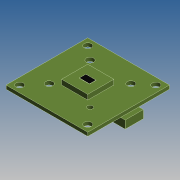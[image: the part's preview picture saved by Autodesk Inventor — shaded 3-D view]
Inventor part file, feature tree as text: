
AUTODESK INVENTOR PART (.ipt)
format: ipt  version: 2015 SP1 (Build 190203100, 203)  size: 267,264 bytes
history: native  units: mm
features: sketch x7, extrude x5, hole x1, pattern_circular x1
ambient origin geometry x8: Origin, YZ Plane, XZ Plane, XY Plane, X Axis, Y Axis, Z Axis, Center Point
bodies: Solid1 (feature_tree)
feature tree (14):
  extrude  "Extrusion1"  Depth=36.0mm
  hole  "Hole1"  [1 undecoded]
  pattern_circular  "Circular Pattern1"  Count=4 Angle=360.0deg
  extrude  "Extrusion2"  Depth=2.88mm
  extrude  "Extrusion3"  Depth=11.5mm
  sketch  "Sketch5"  dims[d16=4.512mm d17=2.88mm]
  extrude  "Extrusion4"  Depth=2.2mm TaperAngle=0.0deg
  extrude  "Extrusion5"  Depth=9.0mm
  sketch  "Sketch1"  dims[d0=36.0mm d1=36.0mm]
  sketch  "Sketch2"  dims[d2=1.6mm d3=0.0mm d4=15.0mm]
  sketch  "Sketch3"  dims[d5=15.0mm]
  sketch  "Sketch4"  dims[d6=3.2mm d7=6.0mm d8=4.0mm d9=2.0mm d10=90.0deg d11=8.0mm d12=20.594885mm d13=40.0mm d14=360.0deg]
  sketch  "Sketch6"  dims[d18=2.3mm d19=0.0mm d20=11.5mm]
  sketch  "Sketch7"  dims[d21=11.5mm d22=2.2mm d23=0.0mm d24=9.0mm d25=8.0mm d26=2.0mm d27=3.5mm d28=0.0mm d44=3.2mm d45=3.2mm d46=3.2mm d47=2.3mm d48=10.0mm d49=10.0mm d50=9.0mm d51=9.0mm d52=8.0mm d53=8.0mm d54=18.0mm d55=18.0mm d56=10.0mm d57=0.0mm d58=18.5mm]
note: 1 required parameter value undecoded (feature->parameter linkage not recoverable at this tier; creation-order binding heuristic only, values carry confidence <= 0.55)
